# Revit family: IC8
name_source: partatom
category: Lighting Fixtures
revit_build: Autodesk Revit Architecture 2012 (Build: 20110309_2315(x64)
units: mm (PartAtom-declared; Revit-internal decimal feet)

## types (4) — shared parameters
Apparent Load = 0 VA
Backbox = White
Ballast = REL-2P32-SC
Color Filter = 16777215
Default Elevation = 48.000"
Description = This premium industrial specification grade fixture has a heavy duty, one piece steel housing with embossed ribs and aperture edges that provide superior rigidity.
Dimming Lamp Color Temperature Shift = <None>
Glass = Glass
Lamp Type = 4', T8: 32, 30, 28 or 25 Watt
Manufacturer = Columbia Lighting
Manufacturer Fax = 866-898-1065
Model = IC8
Product Documentation Link = http://www.columbialighting.com
Product Page URL = http://www.columbialighting.com
Tilt Angle = -90.00°
URL = http://www.columbialighting.com
Voltage = 0 V

## per-type parameters (varying)
| type | Emit from Line Length | Lamp | Photometric Web File | Wattage Comments |
| IC8-232-E | 45.000" | F32T8 | HP05523.IES | 64 |
| IC8-232-VR-E | 24.000" | F32T8 | HP05524.IES | 64 |
| IC8-248HO | 24.000" | F32T8 | HP05432.IES | 64 |
| IC8-332-E-ICFC | 24.000" | 3-F32T8 | HP08922.IES | 87 W |

## geometry (parser evidence)
native form markers: Sweep x1
no freeform markers — native parametric forms only
